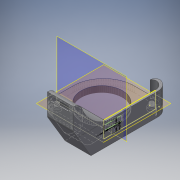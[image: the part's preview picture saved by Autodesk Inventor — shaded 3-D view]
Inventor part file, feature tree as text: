
AUTODESK INVENTOR PART (.ipt)
format: ipt  version: 2016 (Build 200138000, 138)  size: 1,000,448 bytes
history: native  units: mm
features: sketch x8, extrude x6, fillet x5, projected_geometry x5, plane x2, reference x2, imported_body x1, boolean_combine x1, chamfer x1
ambient origin geometry x8: Origin, YZ Plane, XZ Plane, XY Plane, X Axis, Y Axis, Z Axis, Center Point
bodies: Solid1 (feature_tree), Solid2 (feature_tree)
feature tree (31):
  plane  "Work Plane1"
  extrude  "Extrusion1"  Depth=6.1mm
  imported_body  "Base1"
  boolean_combine  "Combine1"
  sketch  "Sketch2"  dims[d3=6.1mm d4=2.0mm d5=0.0mm]
  extrude  "Extrusion2"  Depth=2.0mm TaperAngle=0.0deg
  extrude  "Extrusion3"  Depth=10.0mm
  extrude  "Extrusion4"  TaperAngle=120.0deg  [1 undecoded]
  chamfer  "Chamfer1"  Distance=17.0mm
  extrude  "Extrusion5"  Depth=15.0mm TaperAngle=45.0deg
  sketch  "Sketch7"  dims[d26=10.0mm]
  plane  "Work Plane2"
  extrude  "Extrusion6"  Depth=6.0mm
  fillet  "Fillet1"  Radius=10.0mm
  fillet  "Fillet2"  Radius=1.0mm
  fillet  "Fillet3"  Radius=14.0mm
  fillet  "Fillet4"  Radius=0.8mm
  fillet  "Fillet5"  Radius=13.0mm
  sketch  "Sketch1"  dims[d0=3.0mm d1=0.0mm d2=6.1mm]
  reference  "Reference1"
  reference  "Reference2"
  sketch  "Sketch3"  dims[d6=8.0mm d7=10.0mm]
  projected_geometry  "Projected Loop1"
  sketch  "Sketch4"  dims[d8=2.0mm d9=120.0deg d10=17.0mm d11=0.0mm]
  projected_geometry  "Projected Loop2"
  sketch  "Sketch5"  dims[d12=2.0mm d13=0.0mm d14=15.0mm d15=25.0mm d16=45.0deg]
  projected_geometry  "Projected Loop3"
  sketch  "Sketch6"  dims[d17=2.0mm d18=0.0mm d19=6.0mm d20=10.0mm d21=1.0mm d22=14.0mm d23=0.8mm d24=13.0mm d25=0.0mm]
  projected_geometry  "Projected Loop4"
  projected_geometry  "Projected Loop5"
  sketch  "Sketch8"  dims[d27=10.0mm d28=1.0mm d29=2.0mm d30=2.0mm]
note: 1 required parameter value undecoded (feature->parameter linkage not recoverable at this tier; creation-order binding heuristic only, values carry confidence <= 0.55)
